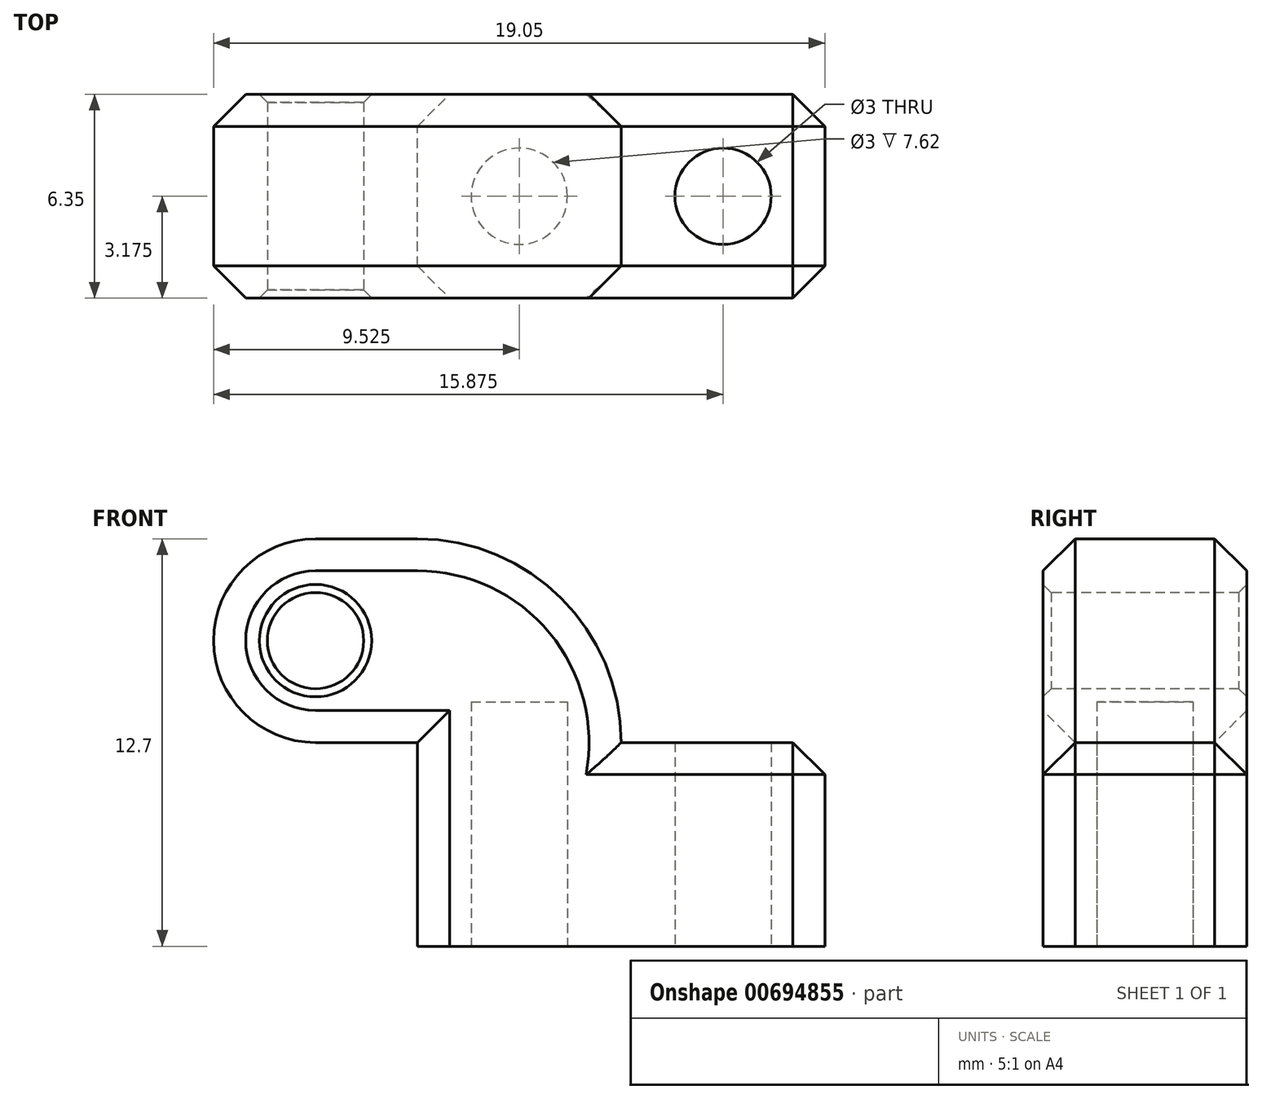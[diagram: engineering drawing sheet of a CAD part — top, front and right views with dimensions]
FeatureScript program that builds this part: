
annotation { "Feature Type Name" : "Feature", "Feature Type Description" : "" }
export const myFeature = defineFeature(function(context is Context, id is Id, definition is map)
    precondition{}
    {
        {
            var Q0;
            Q0=qCreatedBy(makeId("Top.planeOp"),FACE);
            var sketch = newSketch(context, id + "F0", { "sketchPlane" : qUnion([Q0])});
            skLineSegment(sketch, "E0.bottom", {"start": v(0, 0) * mm, "end": v(12.7, 0) * mm});
            skLineSegment(sketch, "E0.top", {"start": v(0, -6.35) * mm, "end": v(12.7, -6.35) * mm});
            skLineSegment(sketch, "E0.left", {"start": v(0, 0) * mm, "end": v(0, -6.35) * mm});
            skLineSegment(sketch, "E0.right", {"start": v(12.7, 0) * mm, "end": v(12.7, -6.35) * mm});
            skSolve(sketch);
        }
        {
            var Q0;
            Q0=qSketchRegion(id+"F0",true);
            extrude(context, id + "F1", {"entities" : qUnion([Q0]), "depth" : 6.35 * mm, "offsetDistance" : 25.4 * mm});
        }
        {
            var Q0;
            Q0=makeQuery(id+"F1.opExtrude","CAP_FACE",FACE,{"disambiguationData":[OSD([sQuery(id+"F0.wireOp",EDGE,"E0.bottom"),sQuery(id+"F0.wireOp",EDGE,"E0.top"),sQuery(id+"F0.wireOp",EDGE,"E0.left"),sQuery(id+"F0.wireOp",EDGE,"E0.right")])],"isStart":false});
            var sketch = newSketch(context, id + "F2", { "sketchPlane" : qUnion([Q0])});
            skLineSegment(sketch, "E1.bottom", {"start": v(0, 0) * mm, "end": v(6.35, 0) * mm});
            skLineSegment(sketch, "E1.top", {"start": v(0, -6.35) * mm, "end": v(6.35, -6.35) * mm});
            skLineSegment(sketch, "E1.left", {"start": v(0, 0) * mm, "end": v(0, -6.35) * mm});
            skLineSegment(sketch, "E1.right", {"start": v(6.35, 0) * mm, "end": v(6.35, -6.35) * mm});
            skSolve(sketch);
        }
        {
            var Q0;
            Q0=qSketchRegion(id+"F2",true);
            extrude(context, id + "F3", {"entities" : qUnion([Q0]), "operationType" : NewBodyOperationType.ADD, "depth" : 6.35 * mm, "offsetDistance" : 25.4 * mm});
        }
        {
            var Q0;
            Q0=makeQuery(id+"F3.boolean.opBoolean","MERGE",FACE,{"derivedFrom":[makeQuery(id+"F1.opExtrude","SWEPT_FACE",FACE,{"disambiguationData":[OSD([sQuery(id+"F0.wireOp",EDGE,"E0.left")])]}),makeQuery(id+"F3.opExtrude","SWEPT_FACE",FACE,{"disambiguationData":[OSD([sQuery(id+"F2.wireOp",EDGE,"E1.left")])]})]});
            var sketch = newSketch(context, id + "F4", { "sketchPlane" : qUnion([Q0])});
            skLineSegment(sketch, "E2.bottom", {"start": v(6.35, 12.7) * mm, "end": v(0, 12.7) * mm});
            skLineSegment(sketch, "E2.top", {"start": v(6.35, 6.35) * mm, "end": v(0, 6.35) * mm});
            skLineSegment(sketch, "E2.left", {"start": v(6.35, 12.7) * mm, "end": v(6.35, 6.35) * mm});
            skLineSegment(sketch, "E2.right", {"start": v(0, 12.7) * mm, "end": v(0, 6.35) * mm});
            skSolve(sketch);
        }
        {
            var Q0;
            Q0=qSketchRegion(id+"F4",true);
            extrude(context, id + "F5", {"entities" : qUnion([Q0]), "operationType" : NewBodyOperationType.ADD, "depth" : 6.35 * mm, "offsetDistance" : 25.4 * mm});
        }
        {
            var Q0;
            Q0=makeQuery(id+"F5.opExtrude","CAP_EDGE",EDGE,{"disambiguationData":[OSD([sQuery(id+"F4.wireOp",EDGE,"E2.bottom")])],"isStart":false});
            var Q1;
            Q1=makeQuery(id+"F5.opExtrude","CAP_EDGE",EDGE,{"disambiguationData":[OSD([sQuery(id+"F4.wireOp",EDGE,"E2.top")])],"isStart":false});
            fillet(context, id + "F6", {"entities" : qUnion([Q0, Q1]), "radius" : 3.17 * mm, "tangentPropagation" : true, "allowEdgeOverflow" : false});
        }
        {
            var Q0;
            Q0=makeQuery(id+"F3.opExtrude","CAP_EDGE",EDGE,{"disambiguationData":[OSD([sQuery(id+"F2.wireOp",EDGE,"E1.right")])],"isStart":false});
            fillet(context, id + "F7", {"entities" : qUnion([Q0]), "radius" : 6.35 * mm, "tangentPropagation" : true, "allowEdgeOverflow" : false});
        }
        {
            var Q0;
            Q0=makeQuery(id+"F5.boolean.opBoolean","MERGE",FACE,{"derivedFrom":[makeQuery(id+"F3.boolean.opBoolean","MERGE",FACE,{"derivedFrom":[makeQuery(id+"F1.opExtrude","SWEPT_FACE",FACE,{"disambiguationData":[OSD([sQuery(id+"F0.wireOp",EDGE,"E0.top")])]}),makeQuery(id+"F3.opExtrude","SWEPT_FACE",FACE,{"disambiguationData":[OSD([sQuery(id+"F2.wireOp",EDGE,"E1.top")])]})]}),makeQuery(id+"F5.opExtrude","SWEPT_FACE",FACE,{"disambiguationData":[OSD([sQuery(id+"F4.wireOp",EDGE,"E2.left")])]})]});
            var sketch = newSketch(context, id + "F8", { "sketchPlane" : qUnion([Q0])});
            skCircle(sketch, "E3", {"center": v(-3.18, 9.53) * mm, "radius": 1.5 * mm});
            skSolve(sketch);
        }
        {
            var Q0;
            Q0=qSketchRegion(id+"F8",true);
            var Q1;
            Q1=makeQuery(id+"F5.boolean.opBoolean","MERGE",FACE,{"derivedFrom":[makeQuery(id+"F3.boolean.opBoolean","MERGE",FACE,{"derivedFrom":[makeQuery(id+"F1.opExtrude","SWEPT_FACE",FACE,{"disambiguationData":[OSD([sQuery(id+"F0.wireOp",EDGE,"E0.bottom")])]}),makeQuery(id+"F3.opExtrude","SWEPT_FACE",FACE,{"disambiguationData":[OSD([sQuery(id+"F2.wireOp",EDGE,"E1.bottom")])]})]}),makeQuery(id+"F5.opExtrude","SWEPT_FACE",FACE,{"disambiguationData":[OSD([sQuery(id+"F4.wireOp",EDGE,"E2.right")])]})]});
            extrude(context, id + "F9", {"entities" : qUnion([Q0]), "operationType" : NewBodyOperationType.REMOVE, "endBound" : BoundingType.UP_TO_SURFACE, "oppositeDirection" : true, "depth" : 25.4 * mm, "endBoundEntityFace" : qUnion([Q1]), "offsetDistance" : 25.4 * mm});
        }
        {
            var Q0;
            Q0=makeQuery(id+"F1.opExtrude","CAP_FACE",FACE,{"disambiguationData":[OSD([sQuery(id+"F0.wireOp",EDGE,"E0.bottom"),sQuery(id+"F0.wireOp",EDGE,"E0.top"),sQuery(id+"F0.wireOp",EDGE,"E0.left"),sQuery(id+"F0.wireOp",EDGE,"E0.right")])],"isStart":true});
            var sketch = newSketch(context, id + "F10", { "sketchPlane" : qUnion([Q0])});
            skCircle(sketch, "E4", {"center": v(9.53, 3.18) * mm, "radius": 1.5 * mm});
            skPoint(sketch, "E4.centerSnap0", {"position": v(12.7, 3.18) * mm});
            skCircle(sketch, "E5", {"center": v(3.18, 3.18) * mm, "radius": 1.5 * mm});
            skPoint(sketch, "E5.centerSnap0", {"position": v(0, 3.18) * mm});
            skSolve(sketch);
        }
        {
            var Q0;
            Q0=qSketchRegion(id+"F10",true);
            extrude(context, id + "F11", {"entities" : qUnion([Q0]), "operationType" : NewBodyOperationType.REMOVE, "oppositeDirection" : true, "depth" : 7.62 * mm, "offsetDistance" : 25.4 * mm});
        }
        {
            var Q0;
            Q0=makeQuery(id+"F9.boolean.opBoolean","COPY",FACE,{"derivedFrom":makeQuery(id+"F9.opExtrude","SWEPT_FACE",FACE,{"disambiguationData":[OSD([sQuery(id+"F8.wireOp",EDGE,"E3")])]})});
            chamfer(context, id + "F12", {"entities" : qUnion([Q0]), "width" : .25 * mm, "tangentPropagation" : true});
        }
        {
            var Q0;
            Q0=makeQuery(id+"F6.opFillet","BLEND_EDGE",EDGE,{"blendedFrom":[makeQuery(id+"F5.opExtrude","CAP_EDGE",EDGE,{"disambiguationData":[OSD([sQuery(id+"F4.wireOp",EDGE,"E2.top")])],"isStart":false}),makeQuery(id+"F5.boolean.opBoolean","MERGE",FACE,{"derivedFrom":[makeQuery(id+"F3.boolean.opBoolean","MERGE",FACE,{"derivedFrom":[makeQuery(id+"F1.opExtrude","SWEPT_FACE",FACE,{"disambiguationData":[OSD([sQuery(id+"F0.wireOp",EDGE,"E0.top")])]}),makeQuery(id+"F3.opExtrude","SWEPT_FACE",FACE,{"disambiguationData":[OSD([sQuery(id+"F2.wireOp",EDGE,"E1.top")])]})]}),makeQuery(id+"F5.opExtrude","SWEPT_FACE",FACE,{"disambiguationData":[OSD([sQuery(id+"F4.wireOp",EDGE,"E2.left")])]})]})],"blendedInto":[makeQuery(id+"F5.boolean.opBoolean","MERGE",FACE,{"derivedFrom":[makeQuery(id+"F3.boolean.opBoolean","MERGE",FACE,{"derivedFrom":[makeQuery(id+"F1.opExtrude","SWEPT_FACE",FACE,{"disambiguationData":[OSD([sQuery(id+"F0.wireOp",EDGE,"E0.top")])]}),makeQuery(id+"F3.opExtrude","SWEPT_FACE",FACE,{"disambiguationData":[OSD([sQuery(id+"F2.wireOp",EDGE,"E1.top")])]})]}),makeQuery(id+"F5.opExtrude","SWEPT_FACE",FACE,{"disambiguationData":[OSD([sQuery(id+"F4.wireOp",EDGE,"E2.left")])]})]})]});
            var Q1;
            Q1=makeQuery(id+"F5.opExtrude","SWEPT_EDGE",EDGE,{"disambiguationData":[OSD([sQuery(id+"F0.wireOp",EDGE,"E0.top"),sQuery(id+"F0.wireOp",EDGE,"E0.left"),sQuery(id+"F2.wireOp",EDGE,"E1.top"),sQuery(id+"F2.wireOp",EDGE,"E1.left"),sQuery(id+"F4.wireOp",EDGE,"E2.top"),sQuery(id+"F4.wireOp",EDGE,"E2.left")])]});
            var Q2;
            Q2=makeQuery(id+"F3.boolean.opBoolean","MERGE",EDGE,{"derivedFrom":[makeQuery(id+"F1.opExtrude","SWEPT_EDGE",EDGE,{"disambiguationData":[OSD([sQuery(id+"F0.wireOp",EDGE,"E0.top"),sQuery(id+"F0.wireOp",EDGE,"E0.left")])]}),makeQuery(id+"F3.opExtrude","SWEPT_EDGE",EDGE,{"disambiguationData":[OSD([sQuery(id+"F2.wireOp",EDGE,"E1.top"),sQuery(id+"F2.wireOp",EDGE,"E1.left")])]})]});
            var Q3;
            Q3=makeQuery(id+"F3.boolean.opBoolean","MERGE",EDGE,{"derivedFrom":[makeQuery(id+"F1.opExtrude","SWEPT_EDGE",EDGE,{"disambiguationData":[OSD([sQuery(id+"F0.wireOp",EDGE,"E0.bottom"),sQuery(id+"F0.wireOp",EDGE,"E0.left")])]}),makeQuery(id+"F3.opExtrude","SWEPT_EDGE",EDGE,{"disambiguationData":[OSD([sQuery(id+"F2.wireOp",EDGE,"E1.bottom"),sQuery(id+"F2.wireOp",EDGE,"E1.left")])]})]});
            var Q4;
            Q4=makeQuery(id+"F6.opFillet","BLEND_EDGE",EDGE,{"blendedFrom":[makeQuery(id+"F5.opExtrude","CAP_EDGE",EDGE,{"disambiguationData":[OSD([sQuery(id+"F4.wireOp",EDGE,"E2.top")])],"isStart":false}),makeQuery(id+"F5.boolean.opBoolean","MERGE",FACE,{"derivedFrom":[makeQuery(id+"F3.boolean.opBoolean","MERGE",FACE,{"derivedFrom":[makeQuery(id+"F1.opExtrude","SWEPT_FACE",FACE,{"disambiguationData":[OSD([sQuery(id+"F0.wireOp",EDGE,"E0.bottom")])]}),makeQuery(id+"F3.opExtrude","SWEPT_FACE",FACE,{"disambiguationData":[OSD([sQuery(id+"F2.wireOp",EDGE,"E1.bottom")])]})]}),makeQuery(id+"F5.opExtrude","SWEPT_FACE",FACE,{"disambiguationData":[OSD([sQuery(id+"F4.wireOp",EDGE,"E2.right")])]})]})],"blendedInto":[makeQuery(id+"F5.boolean.opBoolean","MERGE",FACE,{"derivedFrom":[makeQuery(id+"F3.boolean.opBoolean","MERGE",FACE,{"derivedFrom":[makeQuery(id+"F1.opExtrude","SWEPT_FACE",FACE,{"disambiguationData":[OSD([sQuery(id+"F0.wireOp",EDGE,"E0.bottom")])]}),makeQuery(id+"F3.opExtrude","SWEPT_FACE",FACE,{"disambiguationData":[OSD([sQuery(id+"F2.wireOp",EDGE,"E1.bottom")])]})]}),makeQuery(id+"F5.opExtrude","SWEPT_FACE",FACE,{"disambiguationData":[OSD([sQuery(id+"F4.wireOp",EDGE,"E2.right")])]})]})]});
            var Q5;
            Q5=makeQuery(id+"F5.boolean.opBoolean","MERGE",EDGE,{"derivedFrom":[makeQuery(id+"F3.opExtrude","CAP_EDGE",EDGE,{"disambiguationData":[OSD([sQuery(id+"F2.wireOp",EDGE,"E1.top")])],"isStart":false}),makeQuery(id+"F5.opExtrude","SWEPT_EDGE",EDGE,{"disambiguationData":[OSD([sQuery(id+"F4.wireOp",EDGE,"E2.bottom"),sQuery(id+"F4.wireOp",EDGE,"E2.left")])]})]});
            var Q6;
            Q6=makeQuery(id+"F7.opFillet","BLEND_EDGE",EDGE,{"blendedFrom":[makeQuery(id+"F3.opExtrude","CAP_EDGE",EDGE,{"disambiguationData":[OSD([sQuery(id+"F2.wireOp",EDGE,"E1.right")])],"isStart":false}),makeQuery(id+"F5.boolean.opBoolean","MERGE",FACE,{"derivedFrom":[makeQuery(id+"F3.boolean.opBoolean","MERGE",FACE,{"derivedFrom":[makeQuery(id+"F1.opExtrude","SWEPT_FACE",FACE,{"disambiguationData":[OSD([sQuery(id+"F0.wireOp",EDGE,"E0.top")])]}),makeQuery(id+"F3.opExtrude","SWEPT_FACE",FACE,{"disambiguationData":[OSD([sQuery(id+"F2.wireOp",EDGE,"E1.top")])]})]}),makeQuery(id+"F5.opExtrude","SWEPT_FACE",FACE,{"disambiguationData":[OSD([sQuery(id+"F4.wireOp",EDGE,"E2.left")])]})]})],"blendedInto":[makeQuery(id+"F5.boolean.opBoolean","MERGE",FACE,{"derivedFrom":[makeQuery(id+"F3.boolean.opBoolean","MERGE",FACE,{"derivedFrom":[makeQuery(id+"F1.opExtrude","SWEPT_FACE",FACE,{"disambiguationData":[OSD([sQuery(id+"F0.wireOp",EDGE,"E0.top")])]}),makeQuery(id+"F3.opExtrude","SWEPT_FACE",FACE,{"disambiguationData":[OSD([sQuery(id+"F2.wireOp",EDGE,"E1.top")])]})]}),makeQuery(id+"F5.opExtrude","SWEPT_FACE",FACE,{"disambiguationData":[OSD([sQuery(id+"F4.wireOp",EDGE,"E2.left")])]})]})]});
            var Q7;
            Q7=makeQuery(id+"F1.opExtrude","CAP_EDGE",EDGE,{"disambiguationData":[OSD([sQuery(id+"F0.wireOp",EDGE,"E0.top")])],"isStart":false});
            var Q8;
            Q8=makeQuery(id+"F1.opExtrude","CAP_EDGE",EDGE,{"disambiguationData":[OSD([sQuery(id+"F0.wireOp",EDGE,"E0.bottom")])],"isStart":false});
            var Q9;
            Q9=makeQuery(id+"F1.opExtrude","CAP_EDGE",EDGE,{"disambiguationData":[OSD([sQuery(id+"F0.wireOp",EDGE,"E0.right")])],"isStart":false});
            var Q10;
            Q10=makeQuery(id+"F1.opExtrude","SWEPT_EDGE",EDGE,{"disambiguationData":[OSD([sQuery(id+"F0.wireOp",EDGE,"E0.bottom"),sQuery(id+"F0.wireOp",EDGE,"E0.right")])]});
            var Q11;
            Q11=makeQuery(id+"F1.opExtrude","SWEPT_EDGE",EDGE,{"disambiguationData":[OSD([sQuery(id+"F0.wireOp",EDGE,"E0.top"),sQuery(id+"F0.wireOp",EDGE,"E0.right")])]});
            var Q12;
            Q12=makeQuery(id+"F7.opFillet","BLEND_EDGE",EDGE,{"blendedFrom":[makeQuery(id+"F3.opExtrude","CAP_EDGE",EDGE,{"disambiguationData":[OSD([sQuery(id+"F2.wireOp",EDGE,"E1.right")])],"isStart":false}),makeQuery(id+"F5.boolean.opBoolean","MERGE",FACE,{"derivedFrom":[makeQuery(id+"F3.boolean.opBoolean","MERGE",FACE,{"derivedFrom":[makeQuery(id+"F1.opExtrude","SWEPT_FACE",FACE,{"disambiguationData":[OSD([sQuery(id+"F0.wireOp",EDGE,"E0.bottom")])]}),makeQuery(id+"F3.opExtrude","SWEPT_FACE",FACE,{"disambiguationData":[OSD([sQuery(id+"F2.wireOp",EDGE,"E1.bottom")])]})]}),makeQuery(id+"F5.opExtrude","SWEPT_FACE",FACE,{"disambiguationData":[OSD([sQuery(id+"F4.wireOp",EDGE,"E2.right")])]})]})],"blendedInto":[makeQuery(id+"F5.boolean.opBoolean","MERGE",FACE,{"derivedFrom":[makeQuery(id+"F3.boolean.opBoolean","MERGE",FACE,{"derivedFrom":[makeQuery(id+"F1.opExtrude","SWEPT_FACE",FACE,{"disambiguationData":[OSD([sQuery(id+"F0.wireOp",EDGE,"E0.bottom")])]}),makeQuery(id+"F3.opExtrude","SWEPT_FACE",FACE,{"disambiguationData":[OSD([sQuery(id+"F2.wireOp",EDGE,"E1.bottom")])]})]}),makeQuery(id+"F5.opExtrude","SWEPT_FACE",FACE,{"disambiguationData":[OSD([sQuery(id+"F4.wireOp",EDGE,"E2.right")])]})]})]});
            var Q13;
            Q13=makeQuery(id+"F5.opExtrude","SWEPT_EDGE",EDGE,{"disambiguationData":[OSD([sQuery(id+"F0.wireOp",EDGE,"E0.bottom"),sQuery(id+"F0.wireOp",EDGE,"E0.left"),sQuery(id+"F2.wireOp",EDGE,"E1.bottom"),sQuery(id+"F2.wireOp",EDGE,"E1.left"),sQuery(id+"F4.wireOp",EDGE,"E2.top"),sQuery(id+"F4.wireOp",EDGE,"E2.right")])]});
            var Q14;
            Q14=makeQuery(id+"F5.boolean.opBoolean","MERGE",EDGE,{"derivedFrom":[makeQuery(id+"F3.opExtrude","CAP_EDGE",EDGE,{"disambiguationData":[OSD([sQuery(id+"F2.wireOp",EDGE,"E1.bottom")])],"isStart":false}),makeQuery(id+"F5.opExtrude","SWEPT_EDGE",EDGE,{"disambiguationData":[OSD([sQuery(id+"F4.wireOp",EDGE,"E2.bottom"),sQuery(id+"F4.wireOp",EDGE,"E2.right")])]})]});
            chamfer(context, id + "F13", {"entities" : qUnion([Q0, Q1, Q2, Q3, Q4, Q5, Q6, Q7, Q8, Q9, Q10, Q11, Q12, Q13, Q14]), "width" : 1 * mm, "tangentPropagation" : true});
        }
    });
